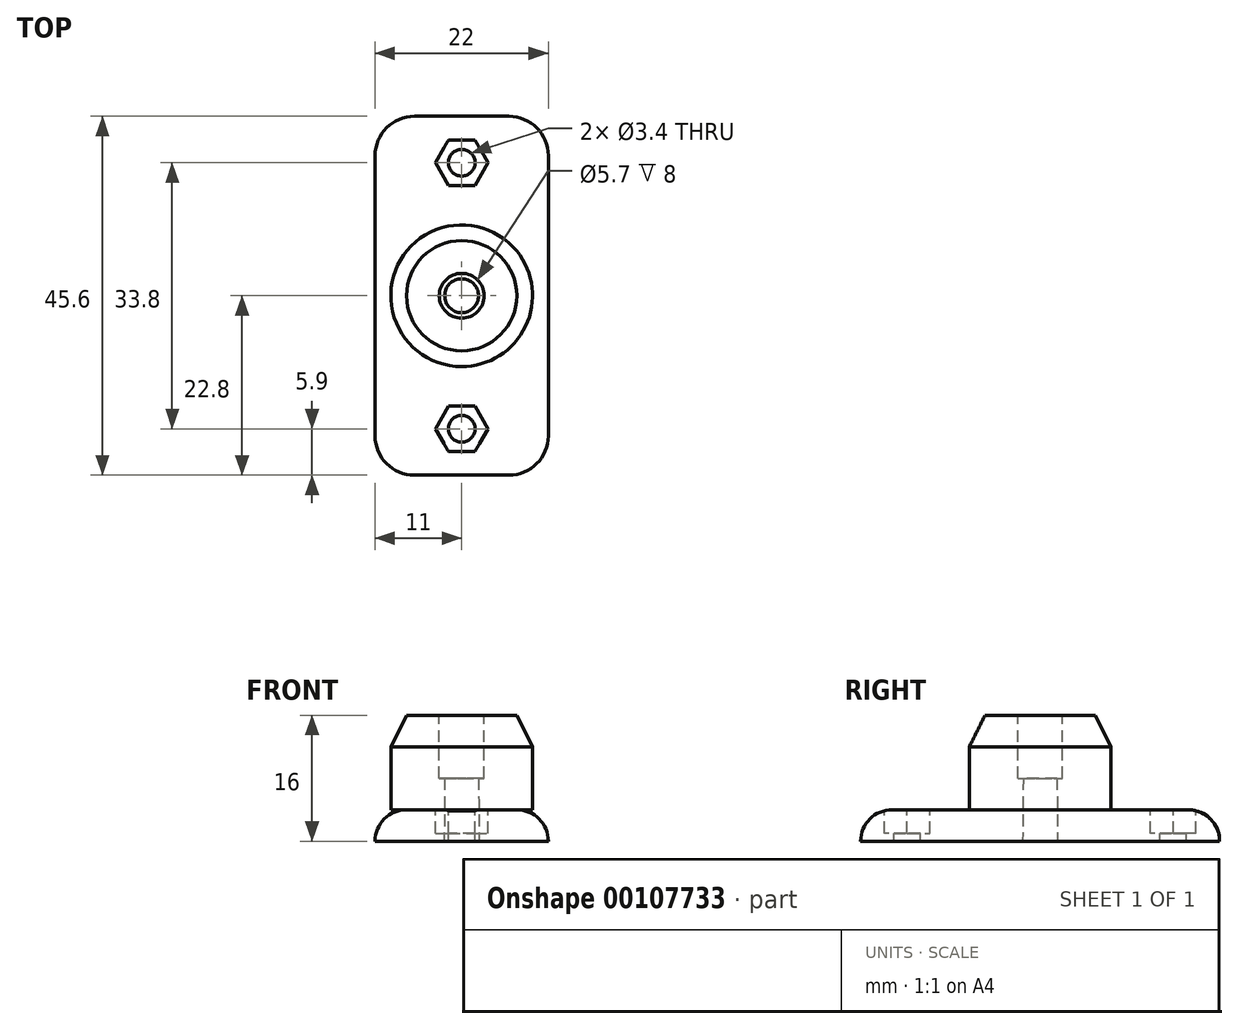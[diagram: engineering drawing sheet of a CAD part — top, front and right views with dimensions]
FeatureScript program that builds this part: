
annotation { "Feature Type Name" : "Feature", "Feature Type Description" : "" }
export const myFeature = defineFeature(function(context is Context, id is Id, definition is map)
    precondition{}
    {
        {
            assignVariable(context, id + "F0", {"name" : "FeederAngle", "anyValue" : 90});
        }
        {
            assignVariable(context, id + "F1", {"name" : "PneumatikThreadDepth", "anyValue" : 8});
        }
        {
            var Q0;
            Q0=qCreatedBy(makeId("Top.planeOp"),FACE);
            var sketch = newSketch(context, id + "F2", { "sketchPlane" : qUnion([Q0])});
            skLineSegment(sketch, "E0.bottom", {"start": v(11, -22.8) * mm, "end": v(-11, -22.8) * mm});
            skLineSegment(sketch, "E0.top", {"start": v(11, 22.8) * mm, "end": v(-11, 22.8) * mm});
            skLineSegment(sketch, "E0.left", {"start": v(11, -22.8) * mm, "end": v(11, 22.8) * mm});
            skLineSegment(sketch, "E0.right", {"start": v(-11, -22.8) * mm, "end": v(-11, 22.8) * mm});
            skPoint(sketch, "E0.middle", {"position": v(0, 0) * mm});
            skLineSegment(sketch, "E1", {"start": v(-11, 0) * mm, "end": v(11, 0) * mm, "construction": true});
            skCircle(sketch, "E2", {"center": v(0, 0) * mm, "radius": 9 * mm, "construction": true});
            skCircle(sketch, "E3.cCircle", {"center": v(0, 16.9) * mm, "radius": 2.9 * mm, "construction": true});
            skLineSegment(sketch, "E3.0", {"start": v(3.35, 16.9) * mm, "end": v(1.67, 14) * mm});
            skLineSegment(sketch, "E3.1", {"start": v(1.67, 14) * mm, "end": v(-1.67, 14) * mm});
            skLineSegment(sketch, "E3.2", {"start": v(-1.67, 14) * mm, "end": v(-3.35, 16.9) * mm});
            skLineSegment(sketch, "E3.3", {"start": v(-3.35, 16.9) * mm, "end": v(-1.67, 19.8) * mm});
            skLineSegment(sketch, "E3.4", {"start": v(-1.67, 19.8) * mm, "end": v(1.67, 19.8) * mm});
            skLineSegment(sketch, "E3.5", {"start": v(1.67, 19.8) * mm, "end": v(3.35, 16.9) * mm});
            skPoint(sketch, "E3.0.midPoint", {"position": v(2.51, 15.45) * mm});
            skCircle(sketch, "E4", {"center": v(0, 0) * mm, "radius": 1.7 * mm});
            skLineSegment(sketch, "E5", {"start": v(0, 22.8) * mm, "end": v(0, -22.8) * mm, "construction": true});
            skLineSegment(sketch, "E6.MirrorCS", {"start": v(1.67, -19.8) * mm, "end": v(3.35, -16.9) * mm});
            skCircle(sketch, "E7.MirrorC", {"center": v(0, -16.9) * mm, "radius": 2.9 * mm, "construction": true});
            skLineSegment(sketch, "E8.MirrorCS", {"start": v(-3.35, -16.9) * mm, "end": v(-1.67, -19.8) * mm});
            skLineSegment(sketch, "E9.MirrorCS", {"start": v(-1.67, -19.8) * mm, "end": v(1.67, -19.8) * mm});
            skLineSegment(sketch, "E10.MirrorCS", {"start": v(3.35, -16.9) * mm, "end": v(1.67, -14) * mm});
            skPoint(sketch, "E11.MirrorP", {"position": v(2.51, -15.45) * mm});
            skLineSegment(sketch, "E12.MirrorCS", {"start": v(-1.67, -14) * mm, "end": v(-3.35, -16.9) * mm});
            skLineSegment(sketch, "E13.MirrorCS", {"start": v(1.67, -14) * mm, "end": v(-1.67, -14) * mm});
            skCircle(sketch, "E14", {"center": v(0, 16.9) * mm, "radius": 1.7 * mm});
            skCircle(sketch, "E15.MirrorC", {"center": v(0, -16.9) * mm, "radius": 1.7 * mm});
            skSolve(sketch);
        }
        {
            var Q0;
            Q0=makeQuery(id+"F2.imprint","IMPRINT",FACE,{"disambiguationData":[TD([[makeQuery(id+"F2.imprint","IMPRINT",EDGE,{"derivedFrom":sQuery(id+"F2.wireOp",EDGE,"E0.bottom")}),-1.0]])]});
            var Q1;
            Q1=makeQuery(id+"F2.imprint","IMPRINT",FACE,{"disambiguationData":[TD([[makeQuery(id+"F2.imprint","IMPRINT",EDGE,{"derivedFrom":sQuery(id+"F2.wireOp",EDGE,"E3.0")}),-1.0]])]});
            var Q2;
            Q2=makeQuery(id+"F2.imprint","IMPRINT",FACE,{"disambiguationData":[TD([[makeQuery(id+"F2.imprint","IMPRINT",EDGE,{"derivedFrom":sQuery(id+"F2.wireOp",EDGE,"bd52aa9b-7235-4a46-b349-5895f92444ec0.MirrorCS")}),1.0]])]});
            var Q3;
            Q3=makeQuery(id+"F2.imprint","IMPRINT",FACE,{"disambiguationData":[TD([[makeQuery(id+"F2.imprint","IMPRINT",EDGE,{"derivedFrom":sQuery(id+"F2.wireOp",EDGE,"E4")}),1.0]])]});
            var Q4;
            Q4=makeQuery(id+"F2.imprint","IMPRINT",FACE,{"disambiguationData":[TD([[makeQuery(id+"F2.imprint","IMPRINT",EDGE,{"derivedFrom":sQuery(id+"F2.wireOp",EDGE,"E6.MirrorCS")}),1.0]])]});
            extrude(context, id + "F3", {"entities" : qUnion([Q0, Q1, Q2, Q3, Q4]), "oppositeDirection" : true, "depth" : 4 * mm});
        }
        {
            var Q0;
            Q0=makeQuery(id+"F3.opExtrude","SWEPT_EDGE",EDGE,{"disambiguationData":[OSD([sQuery(id+"F2.wireOp",EDGE,"E0.top"),sQuery(id+"F2.wireOp",EDGE,"E0.right")])]});
            var Q1;
            Q1=makeQuery(id+"F3.opExtrude","SWEPT_EDGE",EDGE,{"disambiguationData":[OSD([sQuery(id+"F2.wireOp",EDGE,"E0.top"),sQuery(id+"F2.wireOp",EDGE,"E0.left")])]});
            var Q2;
            Q2=makeQuery(id+"F3.opExtrude","SWEPT_EDGE",EDGE,{"disambiguationData":[OSD([sQuery(id+"F2.wireOp",EDGE,"E0.bottom"),sQuery(id+"F2.wireOp",EDGE,"E0.left")])]});
            var Q3;
            Q3=makeQuery(id+"F3.opExtrude","SWEPT_EDGE",EDGE,{"disambiguationData":[OSD([sQuery(id+"F2.wireOp",EDGE,"E0.bottom"),sQuery(id+"F2.wireOp",EDGE,"E0.right")])]});
            fillet(context, id + "F4", {"entities" : qUnion([Q0, Q1, Q2, Q3]), "radius" : 5 * mm, "tangentPropagation" : true, "allowEdgeOverflow" : false});
        }
        {
            var Q0;
            Q0=makeQuery(id+"F3.opExtrude","CAP_EDGE",EDGE,{"disambiguationData":[OSD([sQuery(id+"F2.wireOp",EDGE,"E0.right")])],"isStart":true});
            var Q1;
            Q1=makeQuery(id+"F3.opExtrude","CAP_EDGE",EDGE,{"disambiguationData":[OSD([sQuery(id+"F2.wireOp",EDGE,"E0.bottom")])],"isStart":true});
            var Q2;
            {var subQ0=sQuery(id+"F2.wireOp",EDGE,"E0.right");var subQ1=sQuery(id+"F2.wireOp",EDGE,"E0.bottom");Q2=makeQuery(id+"F4.opFillet","BLEND_EDGE",EDGE,{"blendedFrom":[makeQuery(id+"F3.opExtrude","SWEPT_EDGE",EDGE,{"disambiguationData":[OSD([subQ1,subQ0])]}),makeQuery(id+"F3.opExtrude","CAP_FACE",FACE,{"disambiguationData":[OSD([subQ1,sQuery(id+"F2.wireOp",EDGE,"E0.top"),sQuery(id+"F2.wireOp",EDGE,"E0.left"),subQ0,sQuery(id+"F2.wireOp",EDGE,"E14"),sQuery(id+"F2.wireOp",EDGE,"E15.MirrorC")])],"isStart":true})],"blendedInto":[makeQuery(id+"F3.opExtrude","CAP_FACE",FACE,{"disambiguationData":[OSD([subQ1,sQuery(id+"F2.wireOp",EDGE,"E0.top"),sQuery(id+"F2.wireOp",EDGE,"E0.left"),subQ0,sQuery(id+"F2.wireOp",EDGE,"E14"),sQuery(id+"F2.wireOp",EDGE,"E15.MirrorC")])],"isStart":true})]});}
            var Q3;
            {var subQ0=sQuery(id+"F2.wireOp",EDGE,"E0.left");var subQ1=sQuery(id+"F2.wireOp",EDGE,"E0.bottom");Q3=makeQuery(id+"F4.opFillet","BLEND_EDGE",EDGE,{"blendedFrom":[makeQuery(id+"F3.opExtrude","SWEPT_EDGE",EDGE,{"disambiguationData":[OSD([subQ1,subQ0])]}),makeQuery(id+"F3.opExtrude","CAP_FACE",FACE,{"disambiguationData":[OSD([subQ1,sQuery(id+"F2.wireOp",EDGE,"E0.top"),subQ0,sQuery(id+"F2.wireOp",EDGE,"E0.right"),sQuery(id+"F2.wireOp",EDGE,"E14"),sQuery(id+"F2.wireOp",EDGE,"E15.MirrorC")])],"isStart":true})],"blendedInto":[makeQuery(id+"F3.opExtrude","CAP_FACE",FACE,{"disambiguationData":[OSD([subQ1,sQuery(id+"F2.wireOp",EDGE,"E0.top"),subQ0,sQuery(id+"F2.wireOp",EDGE,"E0.right"),sQuery(id+"F2.wireOp",EDGE,"E14"),sQuery(id+"F2.wireOp",EDGE,"E15.MirrorC")])],"isStart":true})]});}
            var Q4;
            Q4=makeQuery(id+"F3.opExtrude","CAP_EDGE",EDGE,{"disambiguationData":[OSD([sQuery(id+"F2.wireOp",EDGE,"E0.left")])],"isStart":true});
            var Q5;
            {var subQ0=sQuery(id+"F2.wireOp",EDGE,"E0.left");var subQ1=sQuery(id+"F2.wireOp",EDGE,"E0.top");Q5=makeQuery(id+"F4.opFillet","BLEND_EDGE",EDGE,{"blendedFrom":[makeQuery(id+"F3.opExtrude","SWEPT_EDGE",EDGE,{"disambiguationData":[OSD([subQ1,subQ0])]}),makeQuery(id+"F3.opExtrude","CAP_FACE",FACE,{"disambiguationData":[OSD([sQuery(id+"F2.wireOp",EDGE,"E0.bottom"),subQ1,subQ0,sQuery(id+"F2.wireOp",EDGE,"E0.right"),sQuery(id+"F2.wireOp",EDGE,"E14"),sQuery(id+"F2.wireOp",EDGE,"E15.MirrorC")])],"isStart":true})],"blendedInto":[makeQuery(id+"F3.opExtrude","CAP_FACE",FACE,{"disambiguationData":[OSD([sQuery(id+"F2.wireOp",EDGE,"E0.bottom"),subQ1,subQ0,sQuery(id+"F2.wireOp",EDGE,"E0.right"),sQuery(id+"F2.wireOp",EDGE,"E14"),sQuery(id+"F2.wireOp",EDGE,"E15.MirrorC")])],"isStart":true})]});}
            var Q6;
            Q6=makeQuery(id+"F3.opExtrude","CAP_EDGE",EDGE,{"disambiguationData":[OSD([sQuery(id+"F2.wireOp",EDGE,"E0.top")])],"isStart":true});
            var Q7;
            {var subQ0=sQuery(id+"F2.wireOp",EDGE,"E0.right");var subQ1=sQuery(id+"F2.wireOp",EDGE,"E0.top");Q7=makeQuery(id+"F4.opFillet","BLEND_EDGE",EDGE,{"blendedFrom":[makeQuery(id+"F3.opExtrude","SWEPT_EDGE",EDGE,{"disambiguationData":[OSD([subQ1,subQ0])]}),makeQuery(id+"F3.opExtrude","CAP_FACE",FACE,{"disambiguationData":[OSD([sQuery(id+"F2.wireOp",EDGE,"E0.bottom"),subQ1,sQuery(id+"F2.wireOp",EDGE,"E0.left"),subQ0,sQuery(id+"F2.wireOp",EDGE,"E14"),sQuery(id+"F2.wireOp",EDGE,"E15.MirrorC")])],"isStart":true})],"blendedInto":[makeQuery(id+"F3.opExtrude","CAP_FACE",FACE,{"disambiguationData":[OSD([sQuery(id+"F2.wireOp",EDGE,"E0.bottom"),subQ1,sQuery(id+"F2.wireOp",EDGE,"E0.left"),subQ0,sQuery(id+"F2.wireOp",EDGE,"E14"),sQuery(id+"F2.wireOp",EDGE,"E15.MirrorC")])],"isStart":true})]});}
            fillet(context, id + "F5", {"entities" : qUnion([Q0, Q1, Q2, Q3, Q4, Q5, Q6, Q7]), "radius" : 4 * mm, "tangentPropagation" : true, "allowEdgeOverflow" : false});
        }
        {
            var Q0;
            Q0=makeQuery(id+"F2.imprint","IMPRINT",FACE,{"disambiguationData":[TD([[makeQuery(id+"F2.imprint","IMPRINT",EDGE,{"derivedFrom":sQuery(id+"F2.wireOp",EDGE,"E3.0")}),-1.0]])]});
            var Q1;
            Q1=makeQuery(id+"F2.imprint","IMPRINT",FACE,{"disambiguationData":[TD([[makeQuery(id+"F2.imprint","IMPRINT",EDGE,{"derivedFrom":sQuery(id+"F2.wireOp",EDGE,"E6.MirrorCS")}),1.0]])]});
            extrude(context, id + "F6", {"entities" : qUnion([Q0, Q1]), "operationType" : NewBodyOperationType.REMOVE, "oppositeDirection" : true, "depth" : 3 * mm});
        }
        {
            var Q0;
            Q0=sQuery(id+"F2.wireOp",EDGE,"E1");
            cPlane(context, id + "F7", {"entities" : qUnion([Q0]), "cplaneType" : CPlaneType.LINE_ANGLE, "offset" : 150 * mm, "angle" : (getVariable(context, 'FeederAngle')) * degree, "width" : 150 * mm, "height" : 150 * mm});
        }
        {
            var Q0;
            Q0=qCreatedBy(id+"F7.planeOp",FACE);
            var sketch = newSketch(context, id + "F8", { "sketchPlane" : qUnion([Q0])});
            skCircle(sketch, "E16", {"center": v(0, 0) * mm, "radius": 9 * mm});
            skSolve(sketch);
        }
        {
            var Q0;
            Q0=qSketchRegion(id+"F8",true);
            var Q1;
            Q1=makeQuery(id+"F3.opExtrude","CAP_FACE",FACE,{"disambiguationData":[OSD([sQuery(id+"F2.wireOp",EDGE,"E0.bottom"),sQuery(id+"F2.wireOp",EDGE,"E0.top"),sQuery(id+"F2.wireOp",EDGE,"E0.left"),sQuery(id+"F2.wireOp",EDGE,"E0.right"),sQuery(id+"F2.wireOp",EDGE,"E4"),sQuery(id+"F2.wireOp",EDGE,"bd52aa9b-7235-4a46-b349-5895f92444ec8.MirrorC")])],"isStart":true});
            extrude(context, id + "F9", {"entities" : qUnion([Q0]), "operationType" : NewBodyOperationType.ADD, "endBoundEntityFace" : qUnion([Q1]), "depth" : 12 * mm});
        }
        {
            var Q0;
            Q0=makeQuery(id+"F9.opExtrude","CAP_FACE",FACE,{"disambiguationData":[OSD([sQuery(id+"F8.wireOp",EDGE,"E16")])],"isStart":false});
            var sketch = newSketch(context, id + "F10", { "sketchPlane" : qUnion([Q0])});
            skCircle(sketch, "E17", {"center": v(0, 0) * mm, "radius": 2.85 * mm});
            skSolve(sketch);
        }
        {
            var Q0;
            Q0=qSketchRegion(id+"F10",true);
            extrude(context, id + "F11", {"entities" : qUnion([Q0]), "operationType" : NewBodyOperationType.REMOVE, "oppositeDirection" : true, "depth" : (getVariable(context, 'PneumatikThreadDepth')) * mm});
        }
        {
            var Q0;
            Q0=makeQuery(id+"F11.boolean.opBoolean","COPY",FACE,{"derivedFrom":makeQuery(id+"F11.opExtrude","CAP_FACE",FACE,{"disambiguationData":[OSD([sQuery(id+"F10.wireOp",EDGE,"E17")])],"isStart":false})});
            var sketch = newSketch(context, id + "F12", { "sketchPlane" : qUnion([Q0])});
            skCircle(sketch, "E18", {"center": v(0, 0) * mm, "radius": 2.15 * mm});
            skSolve(sketch);
        }
        {
            var Q0;
            Q0=qSketchRegion(id+"F12",true);
            var Q1;
            Q1=makeQuery(id+"F3.opExtrude","CAP_FACE",FACE,{"disambiguationData":[OSD([sQuery(id+"F2.wireOp",EDGE,"E0.bottom"),sQuery(id+"F2.wireOp",EDGE,"E0.top"),sQuery(id+"F2.wireOp",EDGE,"E0.left"),sQuery(id+"F2.wireOp",EDGE,"E0.right"),sQuery(id+"F2.wireOp",EDGE,"E14"),sQuery(id+"F2.wireOp",EDGE,"E15.MirrorC")])],"isStart":false});
            extrude(context, id + "F13", {"entities" : qUnion([Q0]), "operationType" : NewBodyOperationType.REMOVE, "endBound" : BoundingType.UP_TO_SURFACE, "oppositeDirection" : true, "endBoundEntityFace" : qUnion([Q1]), "depth" : 25 * mm, "hasDraft" : true, "draftAngle" : 0.5 * degree});
        }
        {
            var Q0;
            Q0=makeQuery(id+"F9.opExtrude","CAP_EDGE",EDGE,{"disambiguationData":[OSD([sQuery(id+"F8.wireOp",EDGE,"E16")])],"isStart":false});
            chamfer(context, id + "F14", {"entities" : qUnion([Q0]), "chamferType" : ChamferType.TWO_OFFSETS, "width1" : 2 * mm, "oppositeDirection" : false, "width2" : 4 * mm, "tangentPropagation" : true});
        }
    });
